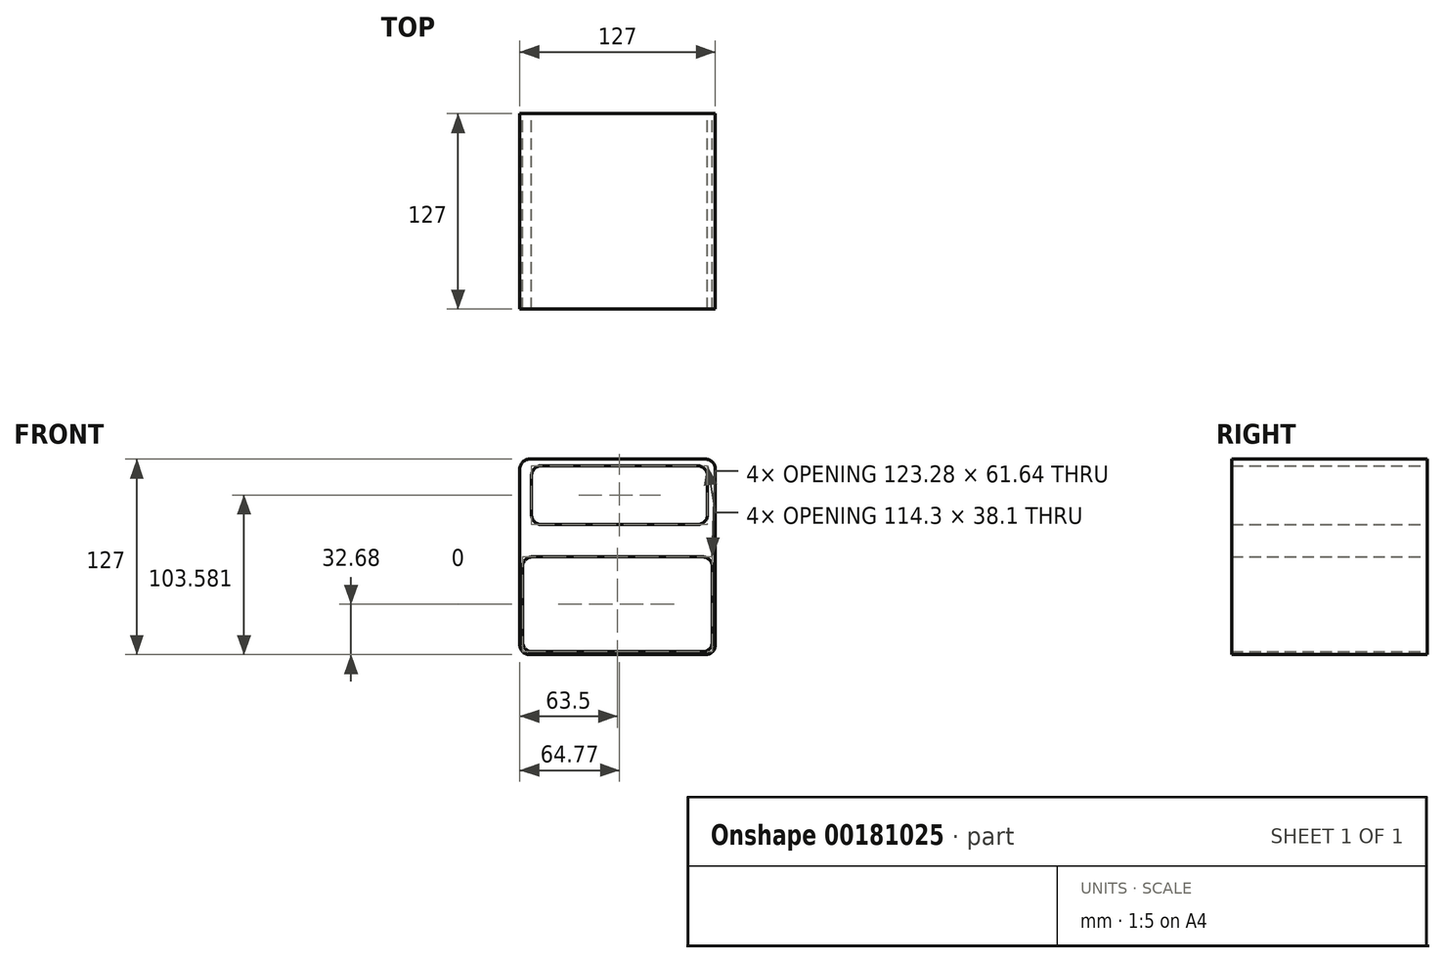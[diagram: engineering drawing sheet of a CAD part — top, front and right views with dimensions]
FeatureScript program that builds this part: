
annotation { "Feature Type Name" : "Feature", "Feature Type Description" : "" }
export const myFeature = defineFeature(function(context is Context, id is Id, definition is map)
    precondition{}
    {
        {
            var Q0;
            Q0=qCreatedBy(makeId("Front.planeOp"),FACE);
            var sketch = newSketch(context, id + "F0", { "sketchPlane" : qUnion([Q0])});
            skLineSegment(sketch, "E0.bottom", {"start": v(57.15, 63.5) * mm, "end": v(-57.15, 63.5) * mm});
            skLineSegment(sketch, "E0.top", {"start": v(57.15, -63.5) * mm, "end": v(-57.15, -63.5) * mm});
            skLineSegment(sketch, "E0.left", {"start": v(63.5, 57.15) * mm, "end": v(63.5, -57.15) * mm});
            skLineSegment(sketch, "E0.right", {"start": v(-63.5, 57.15) * mm, "end": v(-63.5, -57.15) * mm});
            skPoint(sketch, "E0.middle", {"position": v(0, 0) * mm});
            skLineSegment(sketch, "E1.bottom", {"start": v(-49.53, 59.13) * mm, "end": v(52.07, 59.13) * mm});
            skLineSegment(sketch, "E1.top", {"start": v(-49.53, 21.03) * mm, "end": v(52.07, 21.03) * mm});
            skLineSegment(sketch, "E1.left", {"start": v(-55.88, 52.78) * mm, "end": v(-55.88, 27.38) * mm});
            skLineSegment(sketch, "E1.right", {"start": v(58.42, 52.78) * mm, "end": v(58.42, 27.38) * mm});
            skPoint(sketch, "E2.visualSharp", {"position": v(-63.5, 63.5) * mm});
            skArc(sketch, "E2.filletArc", {"start": v(-57.15, 63.5) * mm, "mid": v(-61.64, 61.64) * mm, "end": v(-63.5, 57.15) * mm});
            skPoint(sketch, "E3.visualSharp", {"position": v(-63.5, -63.5) * mm});
            skArc(sketch, "E3.filletArc", {"start": v(-63.5, -57.15) * mm, "mid": v(-61.64, -61.64) * mm, "end": v(-57.15, -63.5) * mm});
            skPoint(sketch, "E4.visualSharp", {"position": v(63.5, -63.5) * mm});
            skArc(sketch, "E4.filletArc", {"start": v(57.15, -63.5) * mm, "mid": v(61.64, -61.64) * mm, "end": v(63.5, -57.15) * mm});
            skPoint(sketch, "E5.visualSharp", {"position": v(63.5, 63.5) * mm});
            skArc(sketch, "E5.filletArc", {"start": v(63.5, 57.15) * mm, "mid": v(61.64, 61.64) * mm, "end": v(57.15, 63.5) * mm});
            skPoint(sketch, "E6.visualSharp", {"position": v(58.42, 21.03) * mm});
            skArc(sketch, "E6.filletArc", {"start": v(52.07, 21.03) * mm, "mid": v(56.56, 22.9) * mm, "end": v(58.42, 27.38) * mm});
            skPoint(sketch, "E7.visualSharp", {"position": v(-55.88, 21.03) * mm});
            skArc(sketch, "E7.filletArc", {"start": v(-55.88, 27.38) * mm, "mid": v(-54.02, 22.9) * mm, "end": v(-49.53, 21.03) * mm});
            skPoint(sketch, "E8.visualSharp", {"position": v(58.42, 59.13) * mm});
            skArc(sketch, "E8.filletArc", {"start": v(58.42, 52.78) * mm, "mid": v(56.56, 57.27) * mm, "end": v(52.07, 59.13) * mm});
            skPoint(sketch, "E9.visualSharp", {"position": v(-55.88, 59.13) * mm});
            skArc(sketch, "E9.filletArc", {"start": v(-49.53, 59.13) * mm, "mid": v(-54.02, 57.27) * mm, "end": v(-55.88, 52.78) * mm});
            skLineSegment(sketch, "E10.bottom", {"start": v(-55.3, -61.64) * mm, "end": v(55.3, -61.64) * mm});
            skLineSegment(sketch, "E10.top", {"start": v(-55.3, 0) * mm, "end": v(55.3, 0) * mm});
            skLineSegment(sketch, "E10.left", {"start": v(-61.64, -55.3) * mm, "end": v(-61.64, -6.35) * mm});
            skLineSegment(sketch, "E10.right", {"start": v(61.64, -55.3) * mm, "end": v(61.64, -6.35) * mm});
            skPoint(sketch, "E10.middle", {"position": v(0, -30.82) * mm});
            skPoint(sketch, "E11.visualSharp", {"position": v(-61.64, -61.64) * mm});
            skArc(sketch, "E11.filletArc", {"start": v(-61.64, -55.3) * mm, "mid": v(-59.78, -59.78) * mm, "end": v(-55.3, -61.64) * mm});
            skPoint(sketch, "E12.visualSharp", {"position": v(61.64, -61.64) * mm});
            skArc(sketch, "E12.filletArc", {"start": v(55.3, -61.64) * mm, "mid": v(59.78, -59.78) * mm, "end": v(61.64, -55.3) * mm});
            skPoint(sketch, "E13.visualSharp", {"position": v(61.64, 0) * mm});
            skArc(sketch, "E13.filletArc", {"start": v(61.64, -6.35) * mm, "mid": v(59.78, -1.86) * mm, "end": v(55.3, 0) * mm});
            skPoint(sketch, "E14.visualSharp", {"position": v(-61.64, 0) * mm});
            skArc(sketch, "E14.filletArc", {"start": v(-55.3, 0) * mm, "mid": v(-59.78, -1.86) * mm, "end": v(-61.64, -6.35) * mm});
            skSolve(sketch);
        }
        {
            var Q0;
            Q0=makeQuery(id+"F0.imprint","IMPRINT",FACE,{"disambiguationData":[TD([[makeQuery(id+"F0.imprint","IMPRINT",EDGE,{"derivedFrom":sQuery(id+"F0.wireOp",EDGE,"E0.bottom")}),1.0]])]});
            extrude(context, id + "F1", {"entities" : qUnion([Q0]), "depth" : 127 * mm});
        }
    });
